# Revit family: g-50_channel_for_gravity_lift_hangover_plug_shine_o30_l450_led_7w__2700k__500ma_810-0390_203a
name_source: partatom
category: Leuchten
revit_build: Autodesk Revit 2016 (Build: 20190508_0715(x64)
units: mm (PartAtom-declared; Revit-internal decimal feet)

## family parameters
Basisbauteil = Fläche
Beim Laden mit Abzugskörper schneiden = Nein
Bemaßung runder Anschluss = Durchmesser verwenden
Gemeinsam genutzt = Nein
Lichtquelle = Nein
Raumberechnungspunkt = Nein
Teiletyp = Normal

## types (1)
- 810-0390-K24 (1 x LED, 448.11 lm, 6.4 W, 2700K)
    Beschreibung = The spot-insert G-50 CHANNEL FOR GRAVITY LIFT / G-50 BOARD FOR GRAVITY LIFT from the familiy G-50 CHANNEL FOR GRAVITY LIFT consists of aluminum. Stated photometric values correspond to operation by 500 mA; a suitable ballast needs to be sourced separately and is not scope of delivery. Dimming (# 810-0390) depends on the used ballast and may vary. The lens based solution shows clear limits and creates sharp contours.
    CIE Flux Codes = 98 99 100 100 73
    Color Rendering = 1A/90…99
    Color Temperature = 2700K
    Height = 0 mm  [stored 0 ft]
    Hersteller = Prolicht
    Lamp Light Flux = 448.11 lm
    Lamp Power = 6.4 W
    Lamp count = 1
    Lampe = 1 x LED
    Length = 28 mm
    Luminous efficacy = 51 lm/W
    ModVariant = Nein
    Modell = 810-0390
    Mounting Place = Ceiling
    Mounting Type = Recessed
    Number of Poles = 1
    OnlyDefault = Ja
    Power Factor = 1
    Product Name = G-50 CHANNEL FOR GRAVITY LIFT__HANGOVER PLUG SHINE Ø30 L450 LED 7W  2700K  500mA
    Product group = Trimless recessed profile systems
    ProductGroupID = 414
    Protection Class = Protection class
    Protection Degree = Degree of protection
    RLX_Detail_Level = 1
    RlxData = <blob elided: 50737 chars, md5=18d94c38>
    Scheinlast = 6 VA
    Socket = socket
    Standby Power = 0 W
    System Light Flux = 326 lm
    System Power = 6 W
    Typenbild = 810-0390.jpg
    URL = http://relux.com
    VarID = 810-0390-k24
    Voltage = 0 V
    Vorgabe-Ansicht = 1800 mm
    Weight = 0.00 kg
    Width = 0 mm  [stored 0 ft]

note: [stored X ft] marks values corroborated as IEEE doubles in the binary element streams (Revit-internal decimal feet)

## geometry (parser evidence)
native form markers: Blend x4, Sweep x14
no freeform markers — native parametric forms only
